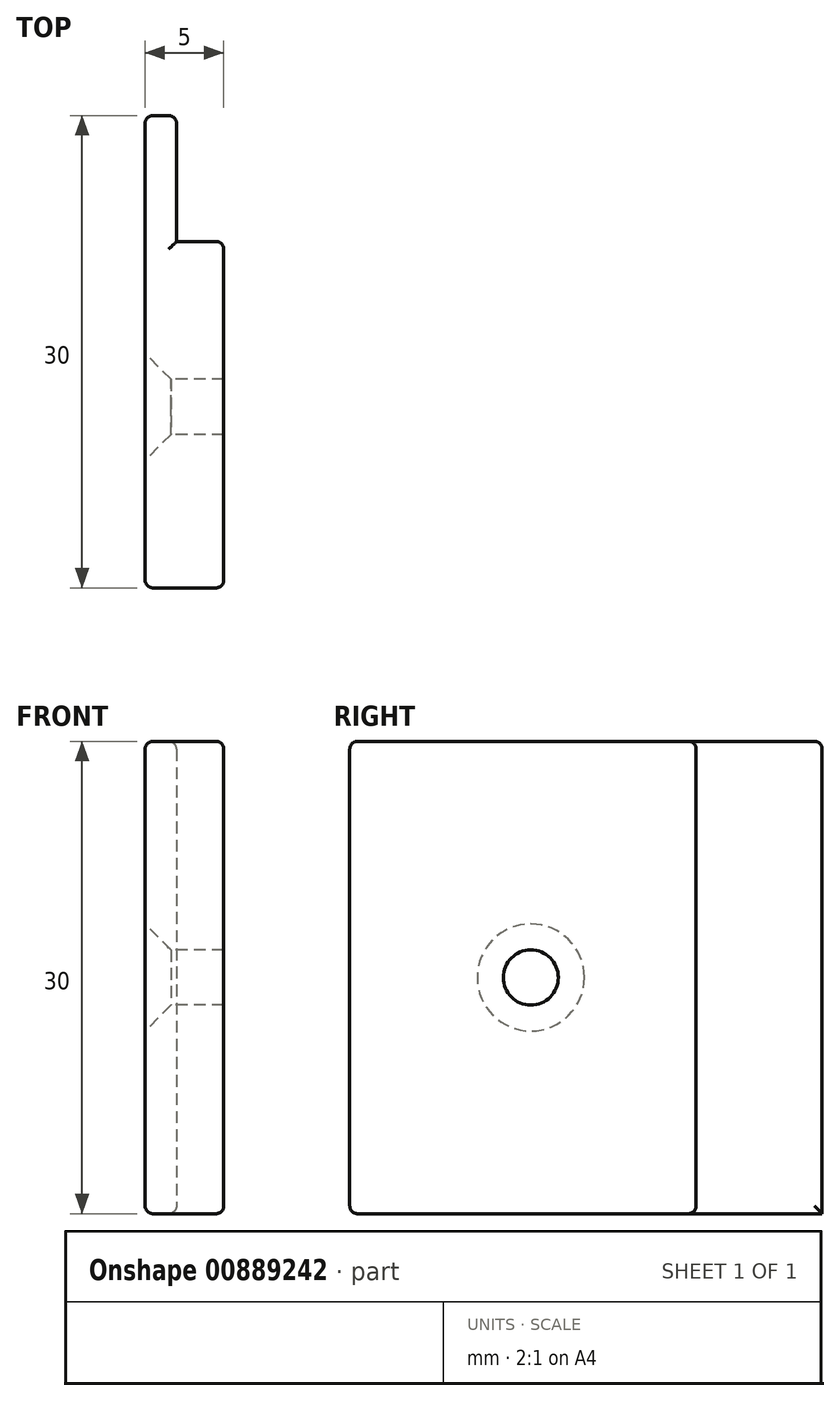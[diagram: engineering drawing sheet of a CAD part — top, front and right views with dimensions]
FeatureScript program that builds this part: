
annotation { "Feature Type Name" : "Feature", "Feature Type Description" : "" }
export const myFeature = defineFeature(function(context is Context, id is Id, definition is map)
    precondition{}
    {
        {
            var Q0;
            Q0=qCreatedBy(makeId("Top.planeOp"),FACE);
            var sketch = newSketch(context, id + "F0", { "sketchPlane" : qUnion([Q0])});
            skLineSegment(sketch, "E0", {"start": v(0, 0) * mm, "end": v(0, 30) * mm});
            skLineSegment(sketch, "E1", {"start": v(0, 30) * mm, "end": v(2, 30) * mm});
            skLineSegment(sketch, "E2", {"start": v(2, 30) * mm, "end": v(2, 22) * mm});
            skLineSegment(sketch, "E3", {"start": v(2, 22) * mm, "end": v(5, 22) * mm});
            skLineSegment(sketch, "E4", {"start": v(5, 0) * mm, "end": v(5, 22) * mm});
            skLineSegment(sketch, "E5", {"start": v(5, 0) * mm, "end": v(0, 0) * mm});
            skSolve(sketch);
        }
        {
            var Q0;
            Q0=makeQuery(id+"F0.imprint","IMPRINT",FACE,{"disambiguationData":[TD([[makeQuery(id+"F0.imprint","IMPRINT",EDGE,{"derivedFrom":sQuery(id+"F0.wireOp",EDGE,"E0")}),-1.0]])]});
            extrude(context, id + "F1", {"entities" : qUnion([Q0]), "depth" : 30 * mm, "offsetDistance" : 25 * mm});
        }
        {
            var Q0;
            Q0=makeQuery(id+"F1.opExtrude","SWEPT_EDGE",EDGE,{"disambiguationData":[OSD([sQuery(id+"F0.wireOp",EDGE,"E1"),sQuery(id+"F0.wireOp",EDGE,"E2")])]});
            var Q1;
            Q1=makeQuery(id+"F1.opExtrude","CAP_EDGE",EDGE,{"disambiguationData":[OSD([sQuery(id+"F0.wireOp",EDGE,"E2")])],"isStart":true});
            var Q2;
            Q2=makeQuery(id+"F1.opExtrude","CAP_EDGE",EDGE,{"disambiguationData":[OSD([sQuery(id+"F0.wireOp",EDGE,"E3")])],"isStart":true});
            var Q3;
            Q3=makeQuery(id+"F1.opExtrude","CAP_EDGE",EDGE,{"disambiguationData":[OSD([sQuery(id+"F0.wireOp",EDGE,"E4")])],"isStart":true});
            var Q4;
            Q4=makeQuery(id+"F1.opExtrude","SWEPT_EDGE",EDGE,{"disambiguationData":[OSD([sQuery(id+"F0.wireOp",EDGE,"E4"),sQuery(id+"F0.wireOp",EDGE,"E5")])]});
            var Q5;
            Q5=makeQuery(id+"F1.opExtrude","CAP_EDGE",EDGE,{"disambiguationData":[OSD([sQuery(id+"F0.wireOp",EDGE,"E2")])],"isStart":false});
            var Q6;
            Q6=makeQuery(id+"F1.opExtrude","SWEPT_EDGE",EDGE,{"disambiguationData":[OSD([sQuery(id+"F0.wireOp",EDGE,"E3"),sQuery(id+"F0.wireOp",EDGE,"E4")])]});
            var Q7;
            Q7=makeQuery(id+"F1.opExtrude","CAP_EDGE",EDGE,{"disambiguationData":[OSD([sQuery(id+"F0.wireOp",EDGE,"E4")])],"isStart":false});
            var Q8;
            Q8=makeQuery(id+"F1.opExtrude","CAP_EDGE",EDGE,{"disambiguationData":[OSD([sQuery(id+"F0.wireOp",EDGE,"E3")])],"isStart":false});
            var Q9;
            Q9=makeQuery(id+"F1.opExtrude","CAP_EDGE",EDGE,{"disambiguationData":[OSD([sQuery(id+"F0.wireOp",EDGE,"E1")])],"isStart":false});
            var Q10;
            Q10=makeQuery(id+"F1.opExtrude","CAP_EDGE",EDGE,{"disambiguationData":[OSD([sQuery(id+"F0.wireOp",EDGE,"E5")])],"isStart":false});
            var Q11;
            Q11=makeQuery(id+"F1.opExtrude","CAP_EDGE",EDGE,{"disambiguationData":[OSD([sQuery(id+"F0.wireOp",EDGE,"E5")])],"isStart":true});
            var Q12;
            Q12=makeQuery(id+"F1.opExtrude","CAP_EDGE",EDGE,{"disambiguationData":[OSD([sQuery(id+"F0.wireOp",EDGE,"E0")])],"isStart":true});
            var Q13;
            Q13=makeQuery(id+"F1.opExtrude","CAP_EDGE",EDGE,{"disambiguationData":[OSD([sQuery(id+"F0.wireOp",EDGE,"E0")])],"isStart":false});
            var Q14;
            Q14=makeQuery(id+"F1.opExtrude","SWEPT_EDGE",EDGE,{"disambiguationData":[OSD([sQuery(id+"F0.wireOp",EDGE,"E0"),sQuery(id+"F0.wireOp",EDGE,"E1")])]});
            var Q15;
            Q15=makeQuery(id+"F1.opExtrude","SWEPT_EDGE",EDGE,{"disambiguationData":[OSD([sQuery(id+"F0.wireOp",EDGE,"E0"),sQuery(id+"F0.wireOp",EDGE,"E5")])]});
            fillet(context, id + "F2", {"entities" : qUnion([Q0, Q1, Q2, Q3, Q4, Q5, Q6, Q7, Q8, Q9, Q10, Q11, Q12, Q13, Q14, Q15]), "radius" : 0.5 * mm, "tangentPropagation" : true, "allowEdgeOverflow" : false});
        }
        {
            var Q0;
            Q0=makeQuery(id+"F1.opExtrude","SWEPT_FACE",FACE,{"disambiguationData":[OSD([sQuery(id+"F0.wireOp",EDGE,"E0")])]});
            var sketch = newSketch(context, id + "F3", { "sketchPlane" : qUnion([Q0])});
            skCircle(sketch, "E6", {"center": v(-11.5, 15) * mm, "radius": 1.75 * mm});
            skPoint(sketch, "E6.centerSnap0", {"position": v(-0.5, 15) * mm});
            skSolve(sketch);
        }
        {
            var Q0;
            Q0=sQuery(id+"F3.wireOp",VERTEX,"E6.center");
            var Q1;
            Q1=makeQuery(id+"F1.opExtrude","SWEPT_BODY",BODY,{"disambiguationData":[OSD([sQuery(id+"F0.wireOp",EDGE,"E0"),sQuery(id+"F0.wireOp",EDGE,"E1"),sQuery(id+"F0.wireOp",EDGE,"E2"),sQuery(id+"F0.wireOp",EDGE,"E3"),sQuery(id+"F0.wireOp",EDGE,"E4"),sQuery(id+"F0.wireOp",EDGE,"E5")])]});
            hole(context, id + "F4", {"style" : HoleStyle.C_SINK, "endStyle" : HoleEndStyle.THROUGH, "holeDiameter" : 3.5 * mm, "cSinkDiameter" : 6.8 * mm, "cSinkAngle" : 90 * degree, "majorDiameter" : 5 * mm, "isTappedThrough" : true, "tappedDepth" : 12 * mm, "tapClearance" : 3, "locations" : qUnion([Q0]), "scope" : qUnion([Q1])});
        }
    });
